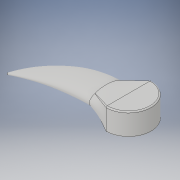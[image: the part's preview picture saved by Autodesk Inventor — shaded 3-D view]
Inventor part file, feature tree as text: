
AUTODESK INVENTOR PART (.ipt)
format: ipt  version: 2019 (Build 230136000, 136)  size: 375,808 bytes
history: native  units: mm
features: other x9, sketch x8, extrude x3, loft x2, fillet x2, revolve x1
ambient origin geometry x8: Origin, YZ Plane, XZ Plane, XY Plane, X Axis, Y Axis, Z Axis, Center Point
bodies: Body1 (feature_tree), Body2 (feature_tree)
feature tree (25):
  other  "хелицера"
  other  "Твердое тело1"
  extrude  "Выдавливание1"  Depth=20.0mm TaperAngle=0.0deg
  other  "РабПлоскость5"
  loft  "Лофт3"
  extrude  "Выдавливание3"  Depth=7.0mm TaperAngle=0.0deg
  other  "РабПлоскость6"
  sketch  "Эскиз11"
  revolve  "Вращение2"
  other  "РабПлоскость7"
  sketch  "Эскиз13"
  other  "РабПлоскость8"
  loft  "Лофт4"
  extrude  "Выдавливание4"  TaperAngle=0.0deg  [1 undecoded]
  fillet  "Сопряжение2"  [1 undecoded]
  fillet  "Сопряжение3"  [1 undecoded]
  sketch  "Эскиз1"
  sketch  "Эскиз9"
  sketch  "Эскиз10"
  other  "Ребра4"
  sketch  "Эскиз12"
  sketch  "Эскиз14"
  other  "Ребра5"
  other  "Ребра6"
  sketch  "Эскиз15"
note: 3 required parameter values undecoded (feature->parameter linkage not recoverable at this tier; creation-order binding heuristic only, values carry confidence <= 0.55)
